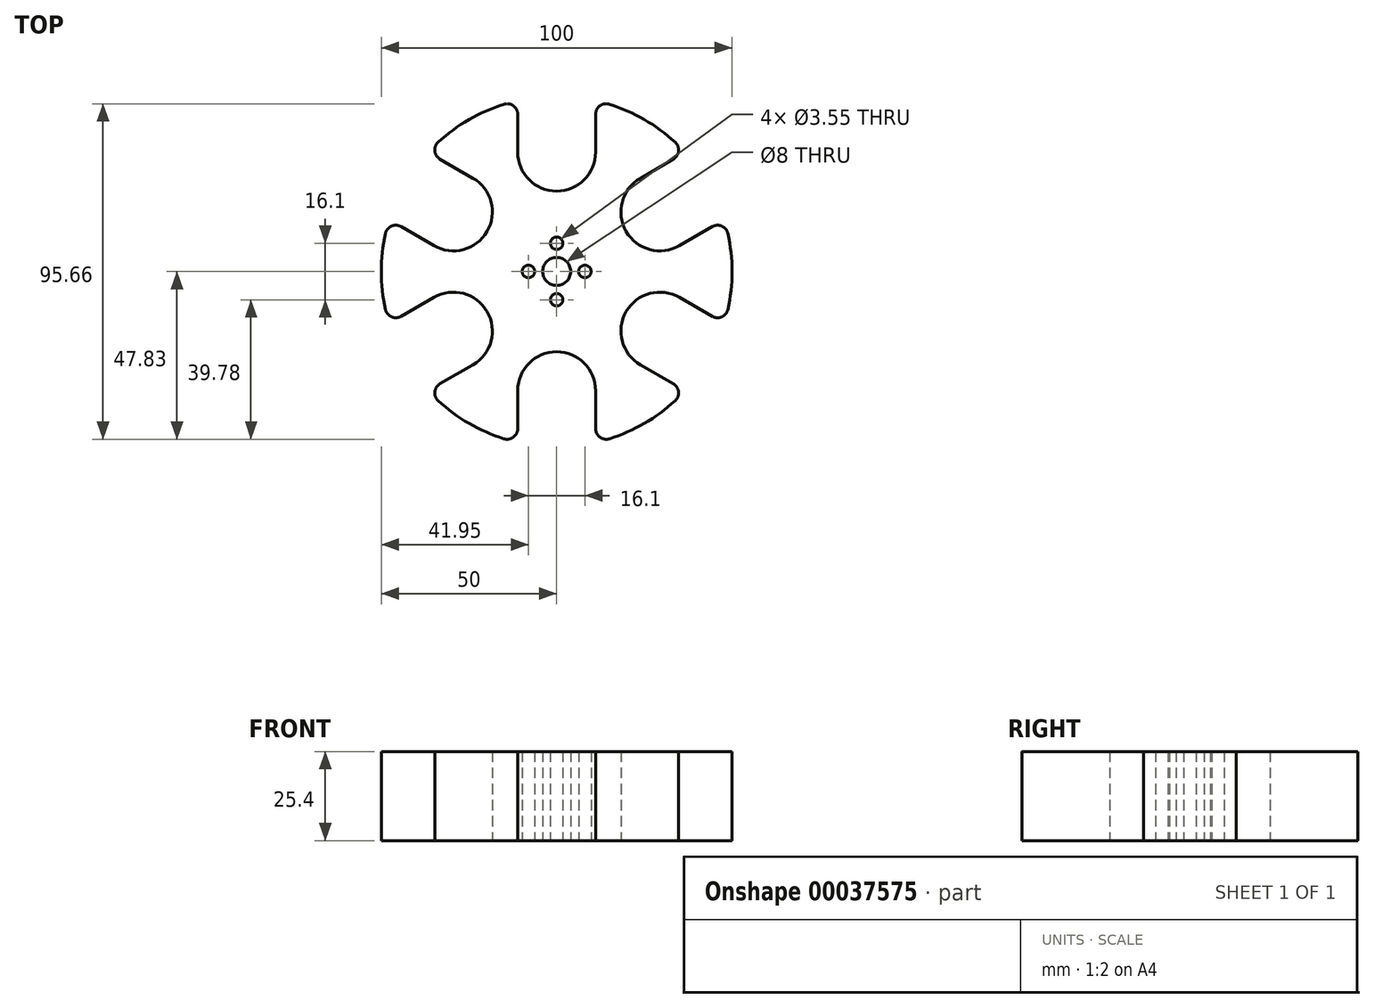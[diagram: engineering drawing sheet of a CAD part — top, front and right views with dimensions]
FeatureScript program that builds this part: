
annotation { "Feature Type Name" : "Feature", "Feature Type Description" : "" }
export const myFeature = defineFeature(function(context is Context, id is Id, definition is map)
    precondition{}
    {
        {
            var Q0;
            Q0=qCreatedBy(makeId("Top.planeOp"),FACE);
            var sketch = newSketch(context, id + "F0", { "sketchPlane" : qUnion([Q0])});
            skArc(sketch, "E0", {"start": v(-15.01, 47.7) * mm, "mid": v(-25, 43.3) * mm, "end": v(-33.8, 36.85) * mm});
            skCircle(sketch, "E1", {"center": v(0, 0) * mm, "radius": 4 * mm});
            skLineSegment(sketch, "E2", {"start": v(0, 0) * mm, "end": v(0, 8.05) * mm, "construction": true});
            skCircle(sketch, "E3", {"center": v(0, 8.05) * mm, "radius": 1.77 * mm});
            skCircle(sketch, "E4.1.0", {"center": v(-8.05, 0) * mm, "radius": 1.77 * mm});
            skCircle(sketch, "E4.2.0", {"center": v(0, -8.05) * mm, "radius": 1.77 * mm});
            skCircle(sketch, "E4.3.0", {"center": v(8.05, 0) * mm, "radius": 1.77 * mm});
            skArc(sketch, "E5", {"start": v(-11.11, 34) * mm, "mid": v(0, 22.89) * mm, "end": v(11.11, 34) * mm});
            skLineSegment(sketch, "E6", {"start": v(-11.11, 34) * mm, "end": v(-11.11, 44.83) * mm});
            skLineSegment(sketch, "E7", {"start": v(11.11, 34) * mm, "end": v(11.11, 44.83) * mm});
            skLineSegment(sketch, "E8.1.0", {"start": v(-35, 7.38) * mm, "end": v(-44.38, 12.8) * mm});
            skArc(sketch, "E8.1.1", {"start": v(-35, 7.38) * mm, "mid": v(-19.82, 11.44) * mm, "end": v(-23.89, 26.62) * mm});
            skLineSegment(sketch, "E8.1.2", {"start": v(-23.89, 26.62) * mm, "end": v(-33.27, 32.04) * mm});
            skLineSegment(sketch, "E8.2.0", {"start": v(-23.89, -26.62) * mm, "end": v(-33.27, -32.04) * mm});
            skArc(sketch, "E8.2.1", {"start": v(-23.89, -26.62) * mm, "mid": v(-19.82, -11.44) * mm, "end": v(-35, -7.38) * mm});
            skLineSegment(sketch, "E8.2.2", {"start": v(-35, -7.38) * mm, "end": v(-44.38, -12.8) * mm});
            skLineSegment(sketch, "E8.3.0", {"start": v(11.11, -34) * mm, "end": v(11.11, -44.83) * mm});
            skArc(sketch, "E8.3.1", {"start": v(11.11, -34) * mm, "mid": v(0, -22.89) * mm, "end": v(-11.11, -34) * mm});
            skLineSegment(sketch, "E8.3.2", {"start": v(-11.11, -34) * mm, "end": v(-11.11, -44.83) * mm});
            skLineSegment(sketch, "E8.4.0", {"start": v(35, -7.38) * mm, "end": v(44.38, -12.8) * mm});
            skArc(sketch, "E8.4.1", {"start": v(35, -7.38) * mm, "mid": v(19.82, -11.44) * mm, "end": v(23.89, -26.62) * mm});
            skLineSegment(sketch, "E8.4.2", {"start": v(23.89, -26.62) * mm, "end": v(33.27, -32.04) * mm});
            skLineSegment(sketch, "E8.5.0", {"start": v(23.89, 26.62) * mm, "end": v(33.27, 32.04) * mm});
            skArc(sketch, "E8.5.1", {"start": v(23.89, 26.62) * mm, "mid": v(19.82, 11.44) * mm, "end": v(35, 7.38) * mm});
            skLineSegment(sketch, "E8.5.2", {"start": v(35, 7.38) * mm, "end": v(44.38, 12.8) * mm});
            skArc(sketch, "E9.trimOffspring", {"start": v(-48.8, 10.84) * mm, "mid": v(-50, 0) * mm, "end": v(-48.8, -10.84) * mm});
            skArc(sketch, "E10.trimOffspring", {"start": v(-33.8, -36.85) * mm, "mid": v(-25, -43.3) * mm, "end": v(-15.01, -47.7) * mm});
            skArc(sketch, "E11.trimOffspring", {"start": v(15.01, -47.7) * mm, "mid": v(25, -43.3) * mm, "end": v(33.8, -36.85) * mm});
            skArc(sketch, "E12.trimOffspring", {"start": v(48.8, -10.84) * mm, "mid": v(50, 0) * mm, "end": v(48.8, 10.84) * mm});
            skArc(sketch, "E13.trimOffspring", {"start": v(33.8, 36.85) * mm, "mid": v(25, 43.3) * mm, "end": v(15.01, 47.7) * mm});
            skPoint(sketch, "E14.visualSharp", {"position": v(11.11, 48.75) * mm});
            skArc(sketch, "E14.filletArc", {"start": v(15.01, 47.7) * mm, "mid": v(12.34, 47.25) * mm, "end": v(11.11, 44.83) * mm});
            skPoint(sketch, "E15.visualSharp", {"position": v(36.66, 34) * mm});
            skArc(sketch, "E15.filletArc", {"start": v(33.27, 32.04) * mm, "mid": v(34.75, 34.31) * mm, "end": v(33.8, 36.85) * mm});
            skPoint(sketch, "E16.visualSharp", {"position": v(47.77, 14.75) * mm});
            skArc(sketch, "E16.filletArc", {"start": v(48.8, 10.84) * mm, "mid": v(47.09, 12.94) * mm, "end": v(44.38, 12.8) * mm});
            skPoint(sketch, "E17.visualSharp", {"position": v(47.77, -14.75) * mm});
            skArc(sketch, "E17.filletArc", {"start": v(44.38, -12.8) * mm, "mid": v(47.09, -12.94) * mm, "end": v(48.8, -10.84) * mm});
            skPoint(sketch, "E18.visualSharp", {"position": v(36.66, -34) * mm});
            skArc(sketch, "E18.filletArc", {"start": v(33.8, -36.85) * mm, "mid": v(34.75, -34.31) * mm, "end": v(33.27, -32.04) * mm});
            skPoint(sketch, "E19.visualSharp", {"position": v(11.11, -48.75) * mm});
            skArc(sketch, "E19.filletArc", {"start": v(11.11, -44.83) * mm, "mid": v(12.34, -47.25) * mm, "end": v(15.01, -47.7) * mm});
            skPoint(sketch, "E20.visualSharp", {"position": v(-11.11, -48.75) * mm});
            skArc(sketch, "E20.filletArc", {"start": v(-15.01, -47.7) * mm, "mid": v(-12.34, -47.25) * mm, "end": v(-11.11, -44.83) * mm});
            skPoint(sketch, "E21.visualSharp", {"position": v(-36.66, -34) * mm});
            skArc(sketch, "E21.filletArc", {"start": v(-33.27, -32.04) * mm, "mid": v(-34.75, -34.31) * mm, "end": v(-33.8, -36.85) * mm});
            skPoint(sketch, "E22.visualSharp", {"position": v(-47.77, -14.75) * mm});
            skArc(sketch, "E22.filletArc", {"start": v(-48.8, -10.84) * mm, "mid": v(-47.09, -12.94) * mm, "end": v(-44.38, -12.8) * mm});
            skPoint(sketch, "E23.visualSharp", {"position": v(-47.77, 14.75) * mm});
            skArc(sketch, "E23.filletArc", {"start": v(-44.38, 12.8) * mm, "mid": v(-47.09, 12.94) * mm, "end": v(-48.8, 10.84) * mm});
            skPoint(sketch, "E24.visualSharp", {"position": v(-36.66, 34) * mm});
            skArc(sketch, "E24.filletArc", {"start": v(-33.8, 36.85) * mm, "mid": v(-34.75, 34.31) * mm, "end": v(-33.27, 32.04) * mm});
            skPoint(sketch, "E25.visualSharp", {"position": v(-11.11, 48.75) * mm});
            skArc(sketch, "E25.filletArc", {"start": v(-11.11, 44.83) * mm, "mid": v(-12.34, 47.25) * mm, "end": v(-15.01, 47.7) * mm});
            skSolve(sketch);
        }
        {
            var Q0;
            Q0=makeQuery(id+"F0.imprint","IMPRINT",FACE,{"disambiguationData":[TD([[makeQuery(id+"F0.imprint","IMPRINT",EDGE,{"derivedFrom":sQuery(id+"F0.wireOp",EDGE,"E0")}),1.0]])]});
            extrude(context, id + "F1", {"entities" : qUnion([Q0]), "depth" : 25.4 * mm});
        }
    });
